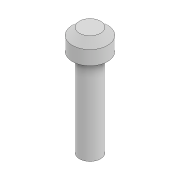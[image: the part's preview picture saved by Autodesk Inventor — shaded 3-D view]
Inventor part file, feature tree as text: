
AUTODESK INVENTOR PART (.ipt)
format: ipt  version: 2022 (Build 260153000, 153)  size: 87,040 bytes
history: native  units: mm
features: extrude x2, sketch x2, chamfer x1
ambient origin geometry x8: Origin, YZ Plane, XZ Plane, XY Plane, X Axis, Y Axis, Z Axis, Center Point
bodies: Solid1 (feature_tree)
feature tree (5):
  extrude  "Extrusion1"  Depth=100.0mm TaperAngle=0.0deg
  extrude  "Extrusion2"  Depth=24.0mm TaperAngle=0.0deg
  chamfer  "Chamfer1"  Distance=8.0mm Angle=45.0deg
  sketch  "Sketch1"  dims[d0=24.0mm d1=100.0mm d2=0.0mm]
  sketch  "Sketch2"  dims[d3=40.0mm d4=24.0mm d5=0.0mm d6=8.0mm d7=2.0mm d8=45.0deg]
